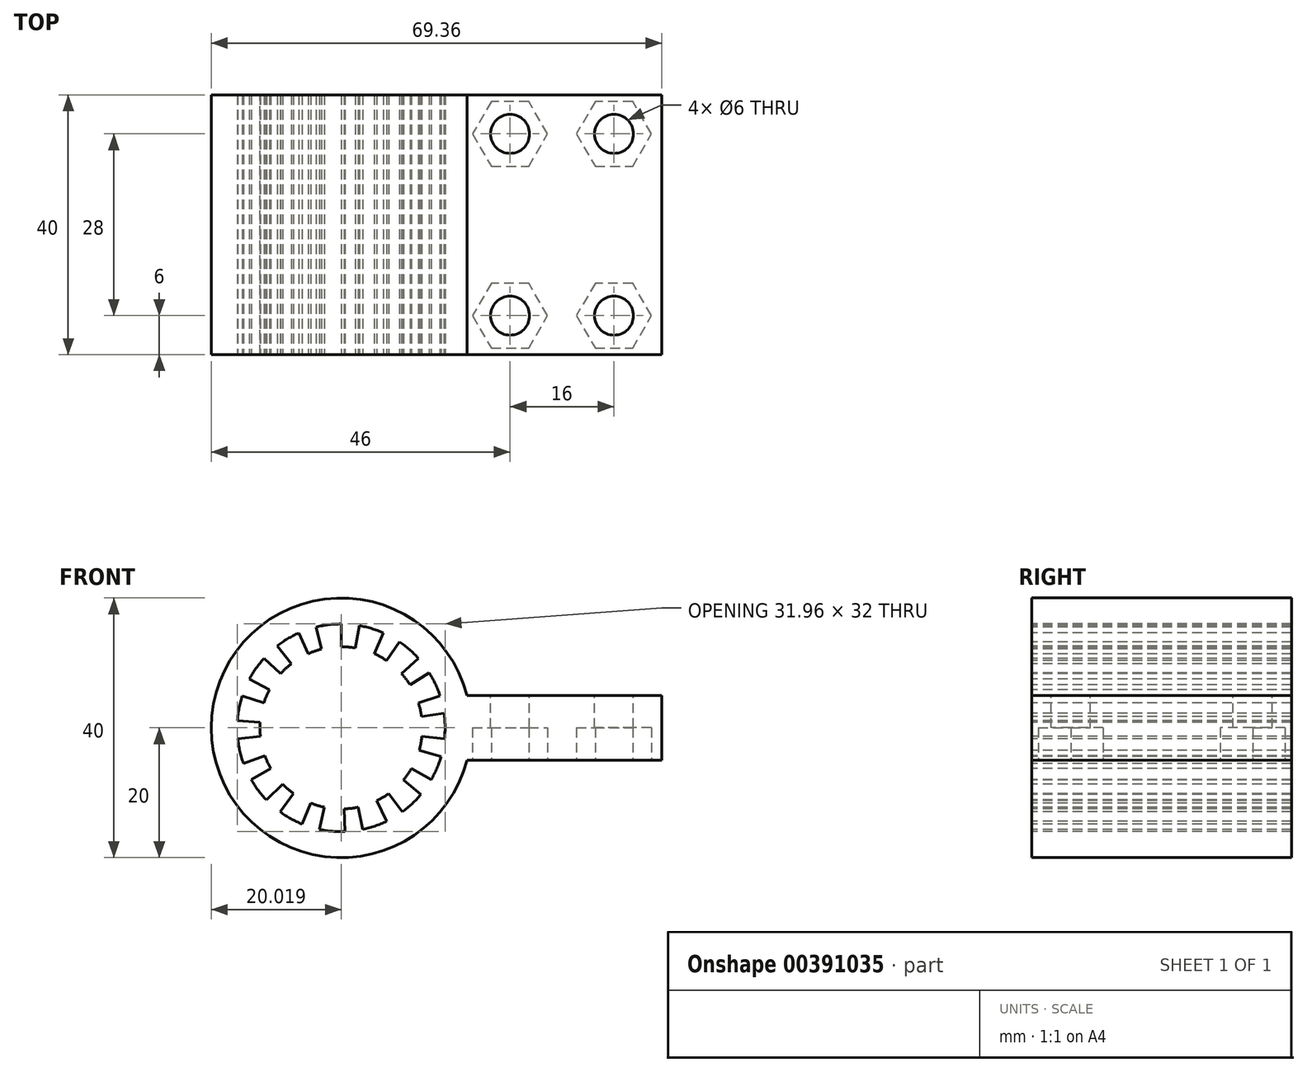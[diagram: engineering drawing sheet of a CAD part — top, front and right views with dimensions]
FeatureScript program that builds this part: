
annotation { "Feature Type Name" : "Feature", "Feature Type Description" : "" }
export const myFeature = defineFeature(function(context is Context, id is Id, definition is map)
    precondition{}
    {
        {
            var Q0;
            Q0=qCreatedBy(makeId("Front.planeOp"),FACE);
            var sketch = newSketch(context, id + "F0", { "sketchPlane" : qUnion([Q0])});
            skCircle(sketch, "E0", {"center": v(0, 0) * mm, "radius": 12.5 * mm});
            skArc(sketch, "E1", {"start": v(19.36, 5) * mm, "mid": v(-20, 0) * mm, "end": v(19.36, -5) * mm});
            skLineSegment(sketch, "E2.bottom", {"start": v(19.36, -5) * mm, "end": v(49.36, -5) * mm});
            skLineSegment(sketch, "E2.top", {"start": v(19.36, 5) * mm, "end": v(49.36, 5) * mm});
            skLineSegment(sketch, "E2.left", {"start": v(19.36, -5) * mm, "end": v(19.36, 5) * mm, "construction": true});
            skLineSegment(sketch, "E2.right", {"start": v(49.36, -5) * mm, "end": v(49.36, 5) * mm});
            skSolve(sketch);
        }
        {
            var Q0;
            Q0 = qSketchRegion(id + "F0", true);
            extrude(context, id + "F1", {"entities" : qUnion([Q0]), "depth" : 20 * mm, "hasSecondDirection" : true, "secondDirectionOppositeDirection" : true, "secondDirectionDepth" : 20 * mm});
        }
        {
            var Q0;
            Q0=makeQuery(id+"F1.opExtrude","CAP_FACE",FACE,{"disambiguationData":[OSD([sQuery(id+"F0.wireOp",EDGE,"E0"),sQuery(id+"F0.wireOp",EDGE,"E1"),sQuery(id+"F0.wireOp",EDGE,"E2.bottom"),sQuery(id+"F0.wireOp",EDGE,"E2.top"),sQuery(id+"F0.wireOp",EDGE,"E2.right")])],"isStart":false});
            var sketch = newSketch(context, id + "F2", { "sketchPlane" : qUnion([Q0])});
            skArc(sketch, "E3", {"start": v(6.5, 14.62) * mm, "mid": v(4.68, 15.3) * mm, "end": v(2.78, 15.76) * mm});
            skLineSegment(sketch, "E4", {"start": v(2.17, 12.31) * mm, "end": v(2.78, 15.76) * mm});
            skLineSegment(sketch, "E5", {"start": v(0, 0) * mm, "end": v(0, 23.52) * mm, "construction": true});
            skArc(sketch, "E6.0", {"start": v(5.08, 11.42) * mm, "mid": v(3.65, 11.95) * mm, "end": v(2.17, 12.31) * mm});
            skLineSegment(sketch, "E7", {"start": v(5.08, 11.42) * mm, "end": v(6.5, 14.62) * mm});
            skLineSegment(sketch, "E8.1.0", {"start": v(-3.02, 12.13) * mm, "end": v(-3.87, 15.52) * mm});
            skArc(sketch, "E8.1.1", {"start": v(0, 16) * mm, "mid": v(-1.95, 15.88) * mm, "end": v(-3.87, 15.52) * mm});
            skArc(sketch, "E8.1.2", {"start": v(0, 12.5) * mm, "mid": v(-1.52, 12.4) * mm, "end": v(-3.02, 12.13) * mm});
            skLineSegment(sketch, "E8.1.3", {"start": v(0, 12.5) * mm, "end": v(0, 16) * mm});
            skLineSegment(sketch, "E8.2.0", {"start": v(-7.7, 9.85) * mm, "end": v(-9.85, 12.6) * mm});
            skArc(sketch, "E8.2.1", {"start": v(-6.5, 14.62) * mm, "mid": v(-8.24, 13.71) * mm, "end": v(-9.85, 12.6) * mm});
            skArc(sketch, "E8.2.2", {"start": v(-5.08, 11.42) * mm, "mid": v(-6.44, 10.71) * mm, "end": v(-7.7, 9.85) * mm});
            skLineSegment(sketch, "E8.2.3", {"start": v(-5.08, 11.42) * mm, "end": v(-6.5, 14.62) * mm});
            skLineSegment(sketch, "E8.3.0", {"start": v(-11.04, 5.87) * mm, "end": v(-14.13, 7.51) * mm});
            skArc(sketch, "E8.3.1", {"start": v(-11.9, 10.7) * mm, "mid": v(-13.1, 9.18) * mm, "end": v(-14.13, 7.51) * mm});
            skArc(sketch, "E8.3.2", {"start": v(-9.29, 8.36) * mm, "mid": v(-10.24, 7.17) * mm, "end": v(-11.04, 5.87) * mm});
            skLineSegment(sketch, "E8.3.3", {"start": v(-9.29, 8.36) * mm, "end": v(-11.9, 10.7) * mm});
            skLineSegment(sketch, "E8.4.0", {"start": v(-12.47, 0.87) * mm, "end": v(-15.96, 1.12) * mm});
            skArc(sketch, "E8.4.1", {"start": v(-15.22, 4.94) * mm, "mid": v(-15.7, 3.05) * mm, "end": v(-15.96, 1.12) * mm});
            skArc(sketch, "E8.4.2", {"start": v(-11.89, 3.86) * mm, "mid": v(-12.27, 2.39) * mm, "end": v(-12.47, 0.87) * mm});
            skLineSegment(sketch, "E8.4.3", {"start": v(-11.89, 3.86) * mm, "end": v(-15.22, 4.94) * mm});
            skLineSegment(sketch, "E8.5.0", {"start": v(-11.75, -4.28) * mm, "end": v(-15.04, -5.47) * mm});
            skArc(sketch, "E8.5.1", {"start": v(-15.91, -1.67) * mm, "mid": v(-15.59, -3.6) * mm, "end": v(-15.04, -5.47) * mm});
            skArc(sketch, "E8.5.2", {"start": v(-12.43, -1.3) * mm, "mid": v(-12.18, -2.81) * mm, "end": v(-11.75, -4.28) * mm});
            skLineSegment(sketch, "E8.5.3", {"start": v(-12.43, -1.3) * mm, "end": v(-15.91, -1.67) * mm});
            skLineSegment(sketch, "E8.6.0", {"start": v(-9, -8.68) * mm, "end": v(-11.5, -11.11) * mm});
            skArc(sketch, "E8.6.1", {"start": v(-13.86, -8) * mm, "mid": v(-12.78, -9.63) * mm, "end": v(-11.5, -11.11) * mm});
            skArc(sketch, "E8.6.2", {"start": v(-10.83, -6.25) * mm, "mid": v(-9.98, -7.52) * mm, "end": v(-9, -8.68) * mm});
            skLineSegment(sketch, "E8.6.3", {"start": v(-10.83, -6.25) * mm, "end": v(-13.86, -8) * mm});
            skLineSegment(sketch, "E8.7.0", {"start": v(-4.68, -11.59) * mm, "end": v(-6, -14.83) * mm});
            skArc(sketch, "E8.7.1", {"start": v(-9.4, -12.94) * mm, "mid": v(-7.76, -14) * mm, "end": v(-6, -14.83) * mm});
            skArc(sketch, "E8.7.2", {"start": v(-7.35, -10.11) * mm, "mid": v(-6.06, -10.93) * mm, "end": v(-4.68, -11.59) * mm});
            skLineSegment(sketch, "E8.7.3", {"start": v(-7.35, -10.11) * mm, "end": v(-9.4, -12.94) * mm});
            skLineSegment(sketch, "E8.8.0", {"start": v(0.44, -12.5) * mm, "end": v(0.56, -16) * mm});
            skArc(sketch, "E8.8.1", {"start": v(-3.33, -15.65) * mm, "mid": v(-1.4, -15.94) * mm, "end": v(0.56, -16) * mm});
            skArc(sketch, "E8.8.2", {"start": v(-2.6, -12.23) * mm, "mid": v(-1.09, -12.45) * mm, "end": v(0.44, -12.5) * mm});
            skLineSegment(sketch, "E8.8.3", {"start": v(-2.6, -12.23) * mm, "end": v(-3.33, -15.65) * mm});
            skLineSegment(sketch, "E8.9.0", {"start": v(5.48, -11.23) * mm, "end": v(7.01, -14.38) * mm});
            skArc(sketch, "E8.9.1", {"start": v(3.33, -15.65) * mm, "mid": v(5.2, -15.13) * mm, "end": v(7.01, -14.38) * mm});
            skArc(sketch, "E8.9.2", {"start": v(2.6, -12.23) * mm, "mid": v(4.07, -11.82) * mm, "end": v(5.48, -11.23) * mm});
            skLineSegment(sketch, "E8.9.3", {"start": v(2.6, -12.23) * mm, "end": v(3.33, -15.65) * mm});
            skLineSegment(sketch, "E8.10.0", {"start": v(9.58, -8.03) * mm, "end": v(12.26, -10.28) * mm});
            skArc(sketch, "E8.10.1", {"start": v(9.4, -12.94) * mm, "mid": v(10.91, -11.7) * mm, "end": v(12.26, -10.28) * mm});
            skArc(sketch, "E8.10.2", {"start": v(7.35, -10.11) * mm, "mid": v(8.52, -9.14) * mm, "end": v(9.58, -8.03) * mm});
            skLineSegment(sketch, "E8.10.3", {"start": v(7.35, -10.11) * mm, "end": v(9.4, -12.94) * mm});
            skLineSegment(sketch, "E8.11.0", {"start": v(12.02, -3.45) * mm, "end": v(15.38, -4.41) * mm});
            skArc(sketch, "E8.11.1", {"start": v(13.86, -8) * mm, "mid": v(14.73, -6.25) * mm, "end": v(15.38, -4.41) * mm});
            skArc(sketch, "E8.11.2", {"start": v(10.83, -6.25) * mm, "mid": v(11.5, -4.88) * mm, "end": v(12.02, -3.45) * mm});
            skLineSegment(sketch, "E8.11.3", {"start": v(10.83, -6.25) * mm, "end": v(13.86, -8) * mm});
            skLineSegment(sketch, "E8.12.0", {"start": v(12.38, 1.74) * mm, "end": v(15.84, 2.23) * mm});
            skArc(sketch, "E8.12.1", {"start": v(15.91, -1.67) * mm, "mid": v(16, 0.28) * mm, "end": v(15.84, 2.23) * mm});
            skArc(sketch, "E8.12.2", {"start": v(12.43, -1.3) * mm, "mid": v(12.5, 0.22) * mm, "end": v(12.38, 1.74) * mm});
            skLineSegment(sketch, "E8.12.3", {"start": v(12.43, -1.3) * mm, "end": v(15.91, -1.67) * mm});
            skLineSegment(sketch, "E8.13.0", {"start": v(10.6, 6.62) * mm, "end": v(13.57, 8.48) * mm});
            skArc(sketch, "E8.13.1", {"start": v(15.22, 4.94) * mm, "mid": v(14.5, 6.76) * mm, "end": v(13.57, 8.48) * mm});
            skArc(sketch, "E8.13.2", {"start": v(11.89, 3.86) * mm, "mid": v(11.33, 5.28) * mm, "end": v(10.6, 6.62) * mm});
            skLineSegment(sketch, "E8.13.3", {"start": v(11.89, 3.86) * mm, "end": v(15.22, 4.94) * mm});
            skLineSegment(sketch, "E8.14.0", {"start": v(6.99, 10.36) * mm, "end": v(8.95, 13.26) * mm});
            skArc(sketch, "E8.14.1", {"start": v(11.9, 10.7) * mm, "mid": v(10.5, 12.08) * mm, "end": v(8.95, 13.26) * mm});
            skArc(sketch, "E8.14.2", {"start": v(9.29, 8.36) * mm, "mid": v(8.2, 9.43) * mm, "end": v(6.99, 10.36) * mm});
            skLineSegment(sketch, "E8.14.3", {"start": v(9.29, 8.36) * mm, "end": v(11.9, 10.7) * mm});
            skSolve(sketch);
        }
        {
            var Q0;
            Q0 = qSketchRegion(id + "F2", true);
            extrude(context, id + "F3", {"entities" : qUnion([Q0]), "operationType" : NewBodyOperationType.REMOVE, "endBound" : BoundingType.THROUGH_ALL, "oppositeDirection" : true, "depth" : 25 * mm});
        }
        {
            var Q0;
            Q0=makeQuery(id+"F1.opExtrude","SWEPT_FACE",FACE,{"disambiguationData":[OSD([sQuery(id+"F0.wireOp",EDGE,"E2.top")])]});
            var sketch = newSketch(context, id + "F4", { "sketchPlane" : qUnion([Q0])});
            skCircle(sketch, "E9", {"center": v(26, 14) * mm, "radius": 3 * mm});
            skCircle(sketch, "E10.1.0.0", {"center": v(42, 14) * mm, "radius": 3 * mm});
            skLineSegment(sketch, "E10.direction1", {"start": v(26, 14) * mm, "end": v(42, 14) * mm, "construction": true});
            skCircle(sketch, "E11.1.0.0", {"center": v(26, -14) * mm, "radius": 3 * mm});
            skCircle(sketch, "E11.1.0.1", {"center": v(42, -14) * mm, "radius": 3 * mm});
            skLineSegment(sketch, "E11.direction1", {"start": v(26, 14) * mm, "end": v(26, -14) * mm, "construction": true});
            skSolve(sketch);
        }
        {
            var Q0;
            Q0 = qSketchRegion(id + "F4", true);
            extrude(context, id + "F5", {"entities" : qUnion([Q0]), "operationType" : NewBodyOperationType.REMOVE, "endBound" : BoundingType.THROUGH_ALL, "oppositeDirection" : true, "depth" : 25 * mm});
        }
        {
            var Q0;
            Q0=makeQuery(id+"F1.opExtrude","SWEPT_FACE",FACE,{"disambiguationData":[OSD([sQuery(id+"F0.wireOp",EDGE,"E2.bottom")])]});
            var sketch = newSketch(context, id + "F6", { "sketchPlane" : qUnion([Q0])});
            skCircle(sketch, "E12.cCircle", {"center": v(26, 14) * mm, "radius": 5 * mm, "construction": true});
            skLineSegment(sketch, "E12.0", {"start": v(28.89, 19) * mm, "end": v(31.77, 14) * mm});
            skLineSegment(sketch, "E12.1", {"start": v(31.77, 14) * mm, "end": v(28.89, 9) * mm});
            skLineSegment(sketch, "E12.2", {"start": v(28.89, 9) * mm, "end": v(23.11, 9) * mm});
            skLineSegment(sketch, "E12.3", {"start": v(23.11, 9) * mm, "end": v(20.23, 14) * mm});
            skLineSegment(sketch, "E12.4", {"start": v(20.23, 14) * mm, "end": v(23.11, 19) * mm});
            skLineSegment(sketch, "E12.5", {"start": v(23.11, 19) * mm, "end": v(28.89, 19) * mm});
            skPoint(sketch, "E12.0.midPoint", {"position": v(30.33, 16.5) * mm});
            skLineSegment(sketch, "E13.1.0.0", {"start": v(44.89, 9) * mm, "end": v(39.11, 9) * mm});
            skLineSegment(sketch, "E13.1.0.1", {"start": v(39.11, 9) * mm, "end": v(36.23, 14) * mm});
            skLineSegment(sketch, "E13.1.0.2", {"start": v(36.23, 14) * mm, "end": v(39.11, 19) * mm});
            skLineSegment(sketch, "E13.1.0.3", {"start": v(39.11, 19) * mm, "end": v(44.89, 19) * mm});
            skLineSegment(sketch, "E13.1.0.4", {"start": v(44.89, 19) * mm, "end": v(47.77, 14) * mm});
            skLineSegment(sketch, "E13.1.0.5", {"start": v(47.77, 14) * mm, "end": v(44.89, 9) * mm});
            skLineSegment(sketch, "E13.direction1", {"start": v(23.11, 9) * mm, "end": v(39.11, 9) * mm, "construction": true});
            skLineSegment(sketch, "E14.1.0.0", {"start": v(36.23, -14) * mm, "end": v(39.11, -9) * mm});
            skLineSegment(sketch, "E14.1.0.1", {"start": v(39.11, -9) * mm, "end": v(44.89, -9) * mm});
            skLineSegment(sketch, "E14.1.0.2", {"start": v(39.11, -19) * mm, "end": v(36.23, -14) * mm});
            skLineSegment(sketch, "E14.1.0.3", {"start": v(44.89, -9) * mm, "end": v(47.77, -14) * mm});
            skLineSegment(sketch, "E14.1.0.4", {"start": v(47.77, -14) * mm, "end": v(44.89, -19) * mm});
            skPoint(sketch, "E14.1.0.5", {"position": v(30.33, -11.5) * mm});
            skLineSegment(sketch, "E14.1.0.6", {"start": v(23.11, -19) * mm, "end": v(39.11, -19) * mm, "construction": true});
            skCircle(sketch, "E14.1.0.7", {"center": v(26, -14) * mm, "radius": 5 * mm, "construction": true});
            skLineSegment(sketch, "E14.1.0.8", {"start": v(44.89, -19) * mm, "end": v(39.11, -19) * mm});
            skLineSegment(sketch, "E14.1.0.9", {"start": v(23.11, -19) * mm, "end": v(20.23, -14) * mm});
            skLineSegment(sketch, "E14.1.0.10", {"start": v(31.77, -14) * mm, "end": v(28.89, -19) * mm});
            skLineSegment(sketch, "E14.1.0.11", {"start": v(28.89, -19) * mm, "end": v(23.11, -19) * mm});
            skLineSegment(sketch, "E14.1.0.12", {"start": v(28.89, -9) * mm, "end": v(31.77, -14) * mm});
            skLineSegment(sketch, "E14.1.0.13", {"start": v(23.11, -9) * mm, "end": v(28.89, -9) * mm});
            skLineSegment(sketch, "E14.1.0.14", {"start": v(20.23, -14) * mm, "end": v(23.11, -9) * mm});
            skLineSegment(sketch, "E14.direction1", {"start": v(23.11, 9) * mm, "end": v(23.11, -19) * mm, "construction": true});
            skSolve(sketch);
        }
        {
            var Q0;
            Q0 = qSketchRegion(id + "F6", true);
            extrude(context, id + "F7", {"entities" : qUnion([Q0]), "operationType" : NewBodyOperationType.REMOVE, "oppositeDirection" : true, "depth" : 5 * mm});
        }
    });
